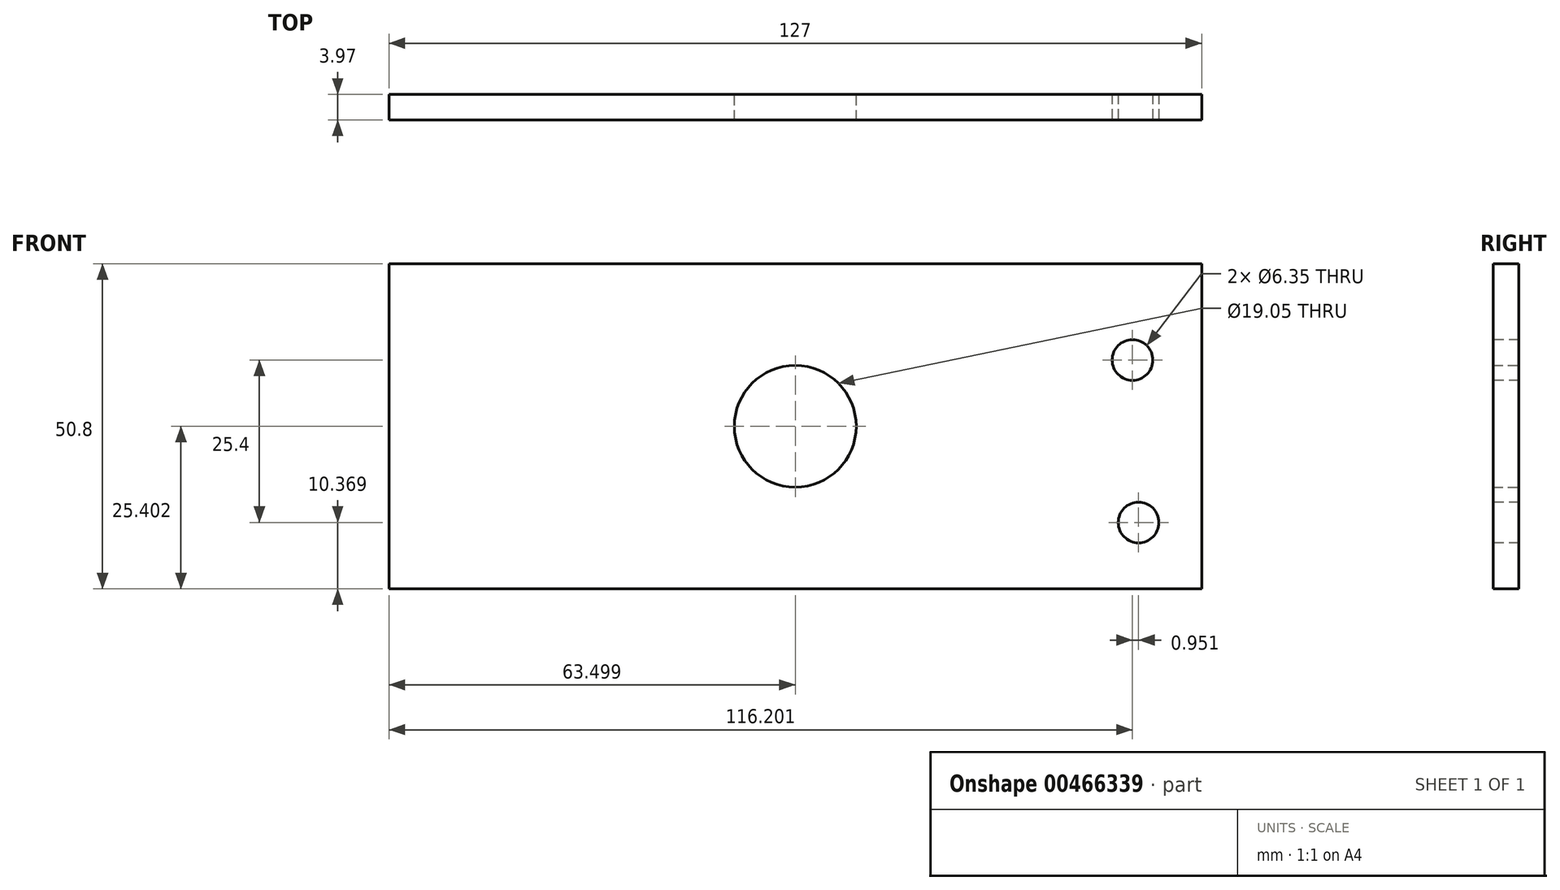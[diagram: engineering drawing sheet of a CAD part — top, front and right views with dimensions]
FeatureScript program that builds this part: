
annotation { "Feature Type Name" : "Feature", "Feature Type Description" : "" }
export const myFeature = defineFeature(function(context is Context, id is Id, definition is map)
    precondition{}
    {
        {
            var Q0;
            Q0=qCreatedBy(makeId("Front.planeOp"),FACE);
            var sketch = newSketch(context, id + "F0", { "sketchPlane" : qUnion([Q0])});
            skLineSegment(sketch, "E0.bottom", {"start": v(-64.13, 16.56) * mm, "end": v(62.87, 16.56) * mm});
            skLineSegment(sketch, "E0.top", {"start": v(-64.13, -34.24) * mm, "end": v(62.87, -34.24) * mm});
            skLineSegment(sketch, "E0.left", {"start": v(-64.13, 16.56) * mm, "end": v(-64.13, -34.24) * mm});
            skLineSegment(sketch, "E0.right", {"start": v(62.87, 16.56) * mm, "end": v(62.87, -34.24) * mm});
            skCircle(sketch, "E1", {"center": v(-0.63, -8.84) * mm, "radius": 9.53 * mm});
            skSolve(sketch);
        }
        {
            var Q0;
            Q0=makeQuery(id+"F0.imprint","IMPRINT",FACE,{"disambiguationData":[TD([[makeQuery(id+"F0.imprint","IMPRINT",EDGE,{"derivedFrom":sQuery(id+"F0.wireOp",EDGE,"E0.bottom")}),-1.0]])]});
            extrude(context, id + "F1", {"entities" : qUnion([Q0]), "depth" : 3.97 * mm});
        }
        {
            var Q0;
            Q0=makeQuery(id+"F1.opExtrude","CAP_FACE",FACE,{"disambiguationData":[OSD([sQuery(id+"F0.wireOp",EDGE,"E0.bottom"),sQuery(id+"F0.wireOp",EDGE,"E0.top"),sQuery(id+"F0.wireOp",EDGE,"E0.left"),sQuery(id+"F0.wireOp",EDGE,"E0.right"),sQuery(id+"F0.wireOp",EDGE,"E1")])],"isStart":false});
            var sketch = newSketch(context, id + "F2", { "sketchPlane" : qUnion([Q0])});
            skCircle(sketch, "E2", {"center": v(52.07, 1.53) * mm, "radius": 3.18 * mm});
            skCircle(sketch, "E3", {"center": v(53.02, -23.87) * mm, "radius": 3.18 * mm});
            skSolve(sketch);
        }
        {
            var Q0;
            Q0=makeQuery(id+"F2.imprint","IMPRINT",FACE,{"disambiguationData":[TD([[makeQuery(id+"F2.imprint","IMPRINT",EDGE,{"derivedFrom":sQuery(id+"F2.wireOp",EDGE,"E2")}),1.0]])]});
            var Q1;
            Q1=makeQuery(id+"F2.imprint","IMPRINT",FACE,{"disambiguationData":[TD([[makeQuery(id+"F2.imprint","IMPRINT",EDGE,{"derivedFrom":sQuery(id+"F2.wireOp",EDGE,"E3")}),1.0]])]});
            extrude(context, id + "F3", {"entities" : qUnion([Q0, Q1]), "operationType" : NewBodyOperationType.REMOVE, "oppositeDirection" : true, "depth" : 25.4 * mm, "symmetric" : true});
        }
    });
